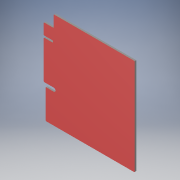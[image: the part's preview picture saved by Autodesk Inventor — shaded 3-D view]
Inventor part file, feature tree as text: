
AUTODESK INVENTOR PART (.ipt)
format: ipt  version: 2018 (Build 220112000, 112)  size: 177,664 bytes
history: native  units: in
note: dims shown in document units (in); Inventor stores cm internally (conversion verified against a paired STEP export)
features: extrude x1, chamfer x1, fillet x1
ambient origin geometry x8: Origin, YZ Plane, XZ Plane, XY Plane, X Axis, Y Axis, Z Axis, Center Point
bodies: Solid1 (feature_tree)
feature tree (3):
  extrude  "Extrusion1"  Depth=2.0197in
  chamfer  "Chamfer1"  Distance=3.7717in
  fillet  "Fillet1"  Radius=0.3937in
